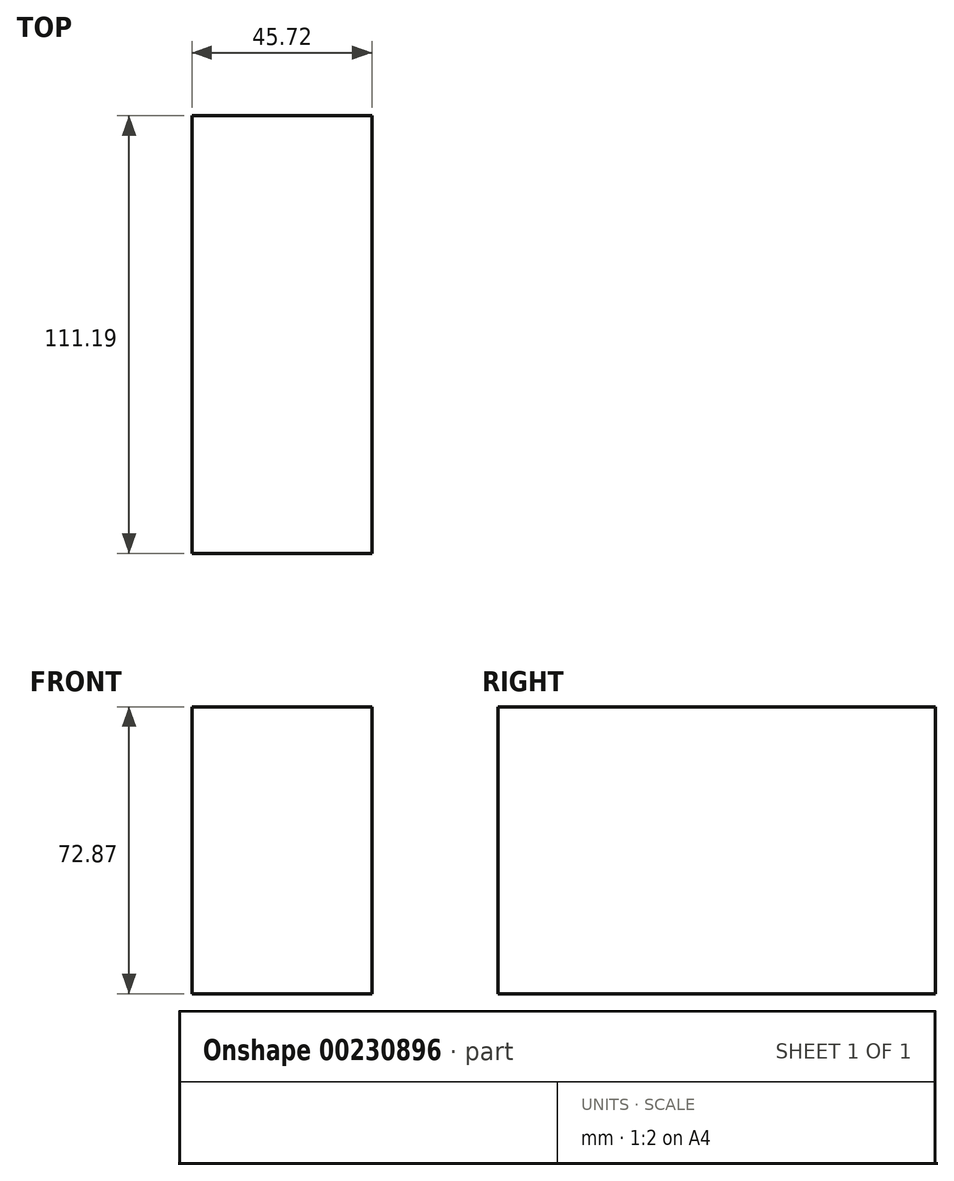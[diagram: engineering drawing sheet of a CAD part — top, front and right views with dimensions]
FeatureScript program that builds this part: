
annotation { "Feature Type Name" : "Feature", "Feature Type Description" : "" }
export const myFeature = defineFeature(function(context is Context, id is Id, definition is map)
    precondition{}
    {
        {
            var Q0;
            Q0=qCreatedBy(makeId("Right.planeOp"),FACE);
            var sketch = newSketch(context, id + "F0", { "sketchPlane" : qUnion([Q0])});
            skLineSegment(sketch, "E0.bottom", {"start": v(-53.78, 36.9) * mm, "end": v(57.41, 36.9) * mm});
            skLineSegment(sketch, "E0.top", {"start": v(-53.78, -35.97) * mm, "end": v(57.41, -35.97) * mm});
            skLineSegment(sketch, "E0.left", {"start": v(-53.78, 36.9) * mm, "end": v(-53.78, -35.97) * mm});
            skLineSegment(sketch, "E0.right", {"start": v(57.41, 36.9) * mm, "end": v(57.41, -35.97) * mm});
            skPoint(sketch, "E1", {"position": v(-110.23, 90.02) * mm});
            skSolve(sketch);
        }
        {
            var Q0;
            Q0=makeQuery(id+"F0.imprint","IMPRINT",FACE,{"disambiguationData":[TD([[makeQuery(id+"F0.imprint","IMPRINT",EDGE,{"derivedFrom":sQuery(id+"F0.wireOp",EDGE,"E0.bottom")}),-1.0]])]});
            extrude(context, id + "F1", {"entities" : qUnion([Q0]), "depth" : 45.72 * mm});
        }
    });
